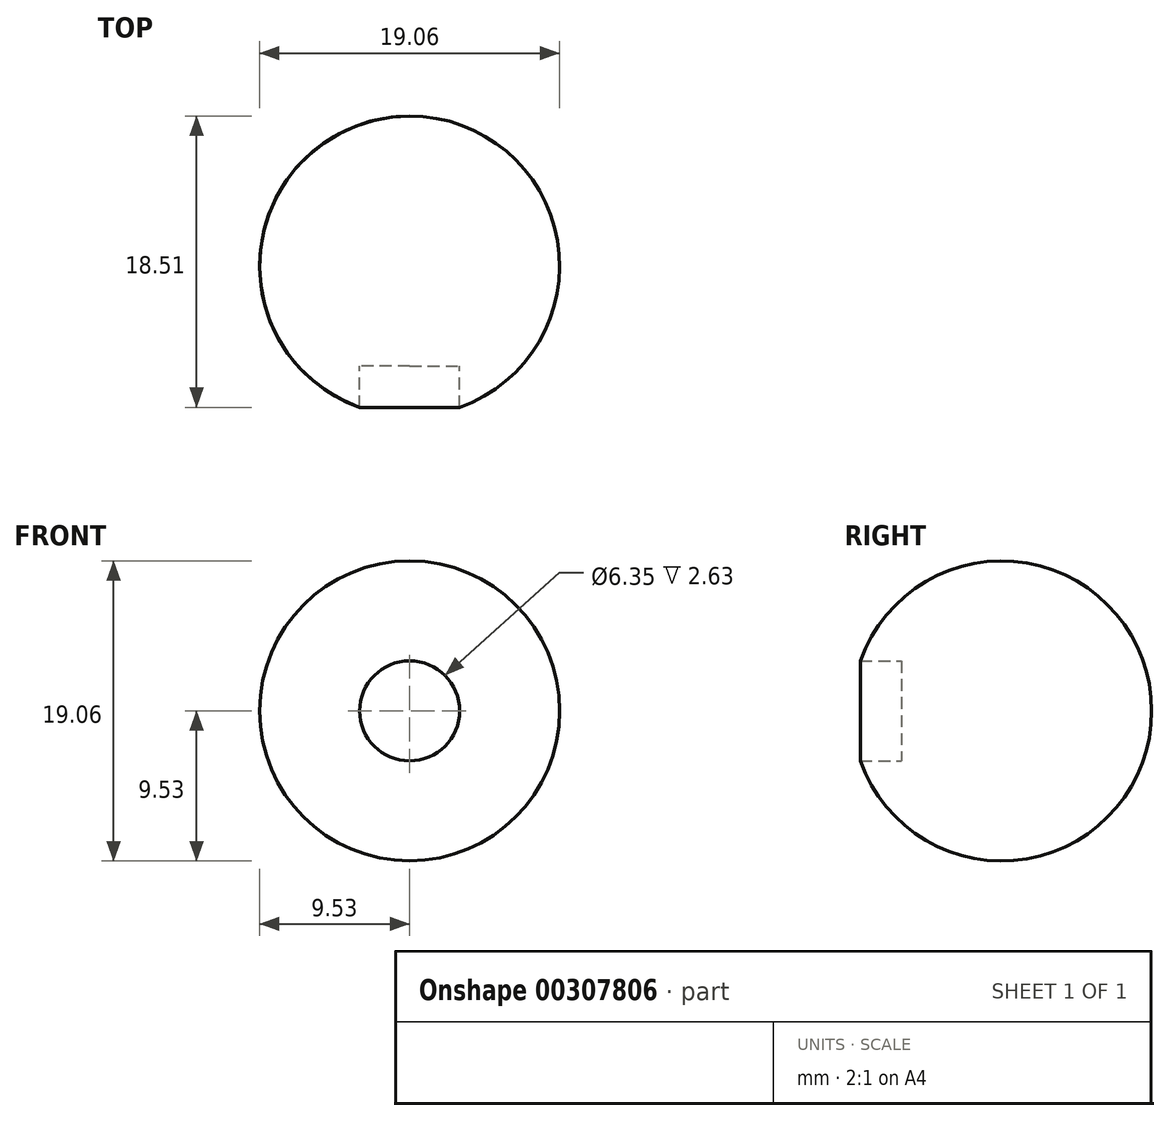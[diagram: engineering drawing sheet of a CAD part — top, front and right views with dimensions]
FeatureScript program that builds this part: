
annotation { "Feature Type Name" : "Feature", "Feature Type Description" : "" }
export const myFeature = defineFeature(function(context is Context, id is Id, definition is map)
    precondition{}
    {
        {
            var Q0;
            Q0=qCreatedBy(makeId("Top.planeOp"),FACE);
            var sketch = newSketch(context, id + "F0", { "sketchPlane" : qUnion([Q0])});
            skArc(sketch, "E0", {"start": v(0, 9.53) * mm, "mid": v(-9.53, 0) * mm, "end": v(0, -9.53) * mm});
            skLineSegment(sketch, "E1", {"start": v(0, 9.53) * mm, "end": v(0, -9.53) * mm});
            skSolve(sketch);
        }
        {
            var Q0;
            Q0=makeQuery(id+"F0.imprint","IMPRINT",FACE,{"disambiguationData":[TD([[makeQuery(id+"F0.imprint","IMPRINT",EDGE,{"derivedFrom":sQuery(id+"F0.wireOp",EDGE,"E0")}),1.0]])]});
            var Q1;
            Q1=sQuery(id+"F0.wireOp",EDGE,"E1");
            revolve(context, id + "F1", {"entities" : qUnion([Q0]), "axis" : qUnion([Q1]), "revolveType" : RevolveType.FULL});
        }
        {
            var Q0;
            Q0=qCreatedBy(makeId("Front.planeOp"),FACE);
            cPlane(context, id + "F2", {"entities" : qUnion([Q0]), "cplaneType" : CPlaneType.OFFSET, "offset" : 6.35 * mm, "width" : 152.4 * mm, "height" : 152.4 * mm});
        }
        {
            var Q0;
            Q0=qCreatedBy(id+"F2.planeOp",FACE);
            var sketch = newSketch(context, id + "F3", { "sketchPlane" : qUnion([Q0])});
            skCircle(sketch, "E2", {"center": v(0, 0) * mm, "radius": 3.18 * mm});
            skSolve(sketch);
        }
        {
            var Q0;
            Q0 = qSketchRegion(id + "F3", true);
            extrude(context, id + "F4", {"entities" : qUnion([Q0]), "depth" : 25.4 * mm});
        }
        {
            var Q0;
            Q0=makeQuery(id+"F4.opExtrude","SWEPT_BODY",BODY,{"disambiguationData":[OSD([sQuery(id+"F3.wireOp",EDGE,"E2")])]});
            var Q1;
            Q1=makeQuery(id+"F1.opRevolve","SWEPT_BODY",BODY,{"disambiguationData":[OSD([sQuery(id+"F0.wireOp",EDGE,"E0"),sQuery(id+"F0.wireOp",EDGE,"E1")])]});
            booleanBodies(context, id + "F5", {"operationType" : BooleanOperationType.SUBTRACTION, "tools" : qUnion([Q0]), "targets" : qUnion([Q1])});
        }
    });
